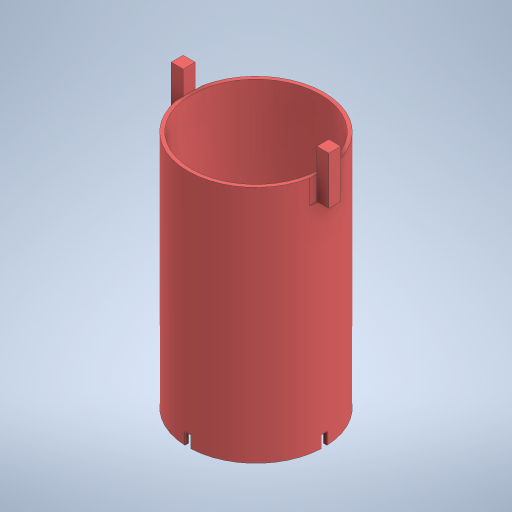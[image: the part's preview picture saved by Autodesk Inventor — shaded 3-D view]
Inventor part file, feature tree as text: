
AUTODESK INVENTOR PART (.ipt)
format: ipt  version: 2024.3 (Build 283343000, 343)  size: 296,960 bytes
history: native  units: mm
features: extrude x4, sketch x4, mirror x1
ambient origin geometry x8: Origin, YZ Plane, XZ Plane, XY Plane, X Axis, Y Axis, Z Axis, Center Point
bodies: Solid1 (feature_tree)
feature tree (9):
  extrude  "Extrusion1"  Depth=114.0mm
  extrude  "Extrusion2"  Depth=200.0mm
  extrude  "Extrusion3"  Depth=40.0mm
  mirror  "Mirror1"
  extrude  "Extrusion4"  Depth=10.0mm
  sketch  "Sketch1"  dims[d0=3.0mm d1=114.0mm]
  sketch  "Sketch2"  dims[d2=200.0mm d3=0.0mm d4=22.0mm]
  sketch  "Sketch3"  dims[d5=20.0mm d6=0.0mm d7=40.0mm]
  sketch  "Sketch4"  dims[d8=10.0mm d9=6.0mm d10=10.0mm d11=0.0mm d12=5.0mm d13=5.0mm d14=120.0mm d15=120.0mm d16=10.0mm d17=0.0mm]
